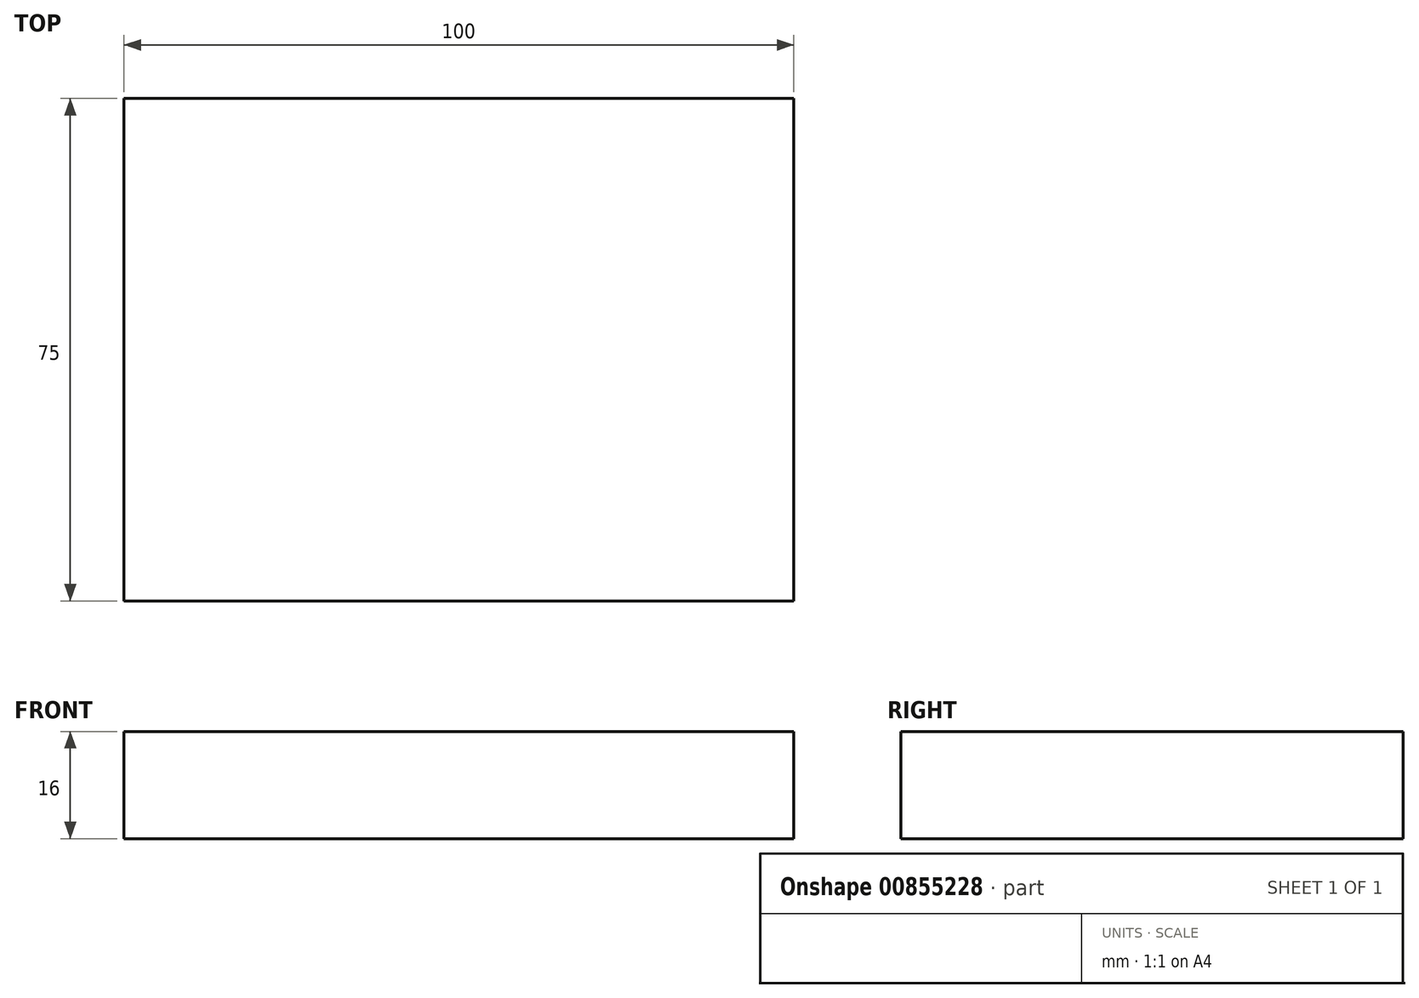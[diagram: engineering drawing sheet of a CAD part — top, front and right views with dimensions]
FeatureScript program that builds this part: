
annotation { "Feature Type Name" : "Feature", "Feature Type Description" : "" }
export const myFeature = defineFeature(function(context is Context, id is Id, definition is map)
    precondition{}
    {
        {
            var Q0;
            Q0=qCreatedBy(makeId("Top.planeOp"),FACE);
            var sketch = newSketch(context, id + "F0", { "sketchPlane" : qUnion([Q0])});
            skLineSegment(sketch, "E0.bottom", {"start": v(0, 0) * mm, "end": v(100, 0) * mm});
            skLineSegment(sketch, "E0.top", {"start": v(0, 75) * mm, "end": v(100, 75) * mm});
            skLineSegment(sketch, "E0.left", {"start": v(0, 0) * mm, "end": v(0, 75) * mm});
            skLineSegment(sketch, "E0.right", {"start": v(100, 0) * mm, "end": v(100, 75) * mm});
            skSolve(sketch);
        }
        {
            var Q0;
            Q0=qSketchRegion(id+"F0",true);
            extrude(context, id + "F1", {"entities" : qUnion([Q0]), "depth" : 16 * mm, "offsetDistance" : 25 * mm});
        }
    });
